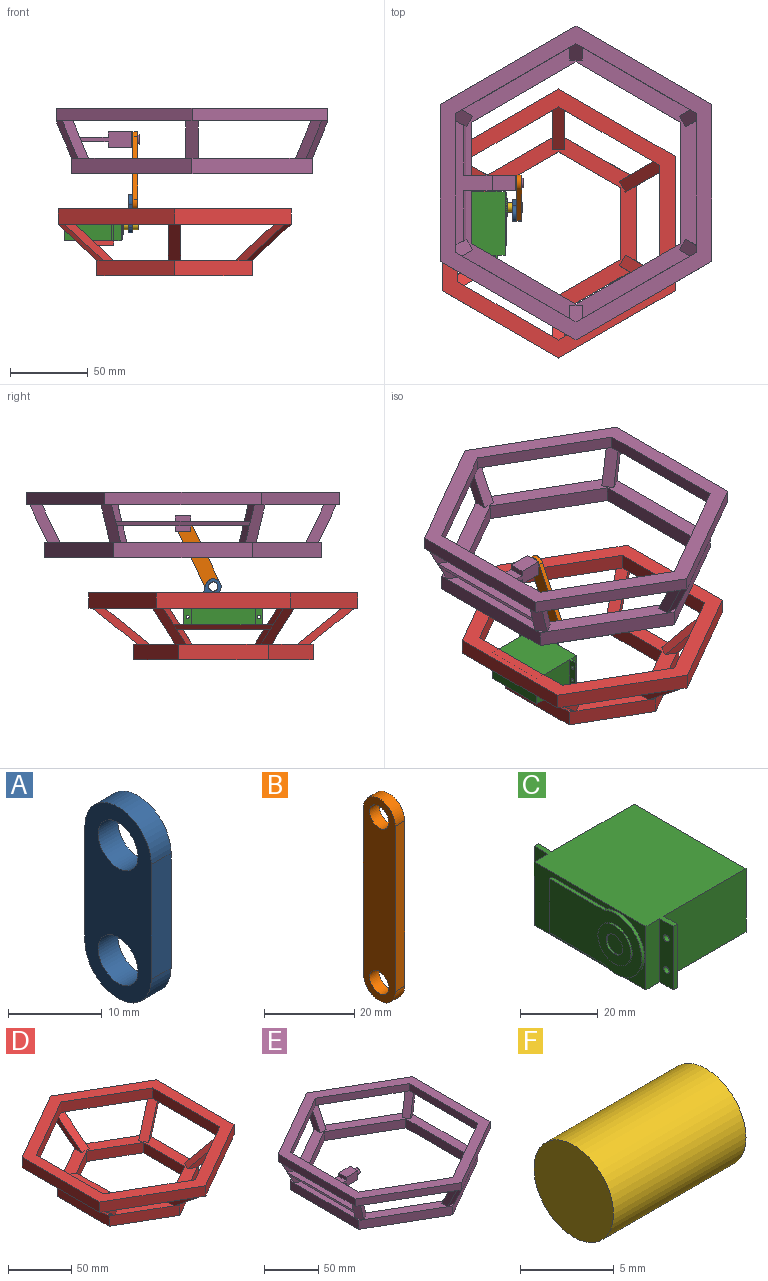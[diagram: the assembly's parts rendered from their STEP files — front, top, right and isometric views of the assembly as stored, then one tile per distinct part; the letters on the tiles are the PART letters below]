
ASSEMBLY  parts=6 mates=6
PART A: 8 faces, bbox 3x10x25 mm
  f0: plane 15x3mm, normal (0,1,0), area 45mm2, adj f1,f5,f6,f7
  f1: cylinder r=5mm len=10mm, axis (-1,0,0), area 47.1mm2, adj f0,f2,f6,f7
  f2: plane 15x3mm, normal (0,-1,0), area 45mm2, adj f1,f5,f6,f7
  f3: cylinder r=3mm len=6mm, axis (-1,0,0), area 56.5mm2, adj f6,f7
  f4: cylinder r=3mm len=6mm, axis (-1,0,0), area 56.5mm2, adj f6,f7
  f5: cylinder r=5mm len=10mm, axis (-1,0,0), area 47.1mm2, adj f0,f2,f6,f7
  f6: plane 25x10mm, normal (1,0,0), area 172mm2, adj f0,f1,f2,f3,f4,f5
  f7: plane 25x10mm, normal (-1,0,0), area 172mm2, adj f0,f1,f2,f3,f4,f5
PART B: 8 faces, bbox 3x10x55 mm
  f0: plane 45x3mm, normal (0,1,0), area 135mm2, adj f1,f5,f6,f7
  f1: cylinder r=5mm len=10mm, axis (-1,0,0), area 47.1mm2, adj f0,f2,f6,f7
  f2: plane 45x3mm, normal (0,-1,0), area 135mm2, adj f1,f5,f6,f7
  f3: cylinder r=3mm len=6mm, axis (-1,0,0), area 56.5mm2, adj f6,f7
  f4: cylinder r=3mm len=6mm, axis (-1,0,0), area 56.5mm2, adj f6,f7
  f5: cylinder r=5mm len=10mm, axis (-1,0,0), area 47.1mm2, adj f0,f2,f6,f7
  f6: plane 55x10mm, normal (1,0,0), area 472mm2, adj f0,f1,f2,f3,f4,f5
  f7: plane 55x10mm, normal (-1,0,0), area 472mm2, adj f0,f1,f2,f3,f4,f5
PART C: 27 faces, bbox 38x50.8x20 mm
  f0: plane 20x5mm, normal (0,1,0), area 100mm2, adj f2,f3,f4,f22
  f1: plane 20x5mm, normal (0,-1,0), area 100mm2, adj f2,f3,f4,f19
  f2: plane 40.8x20mm, normal (-1,0,0), area 256.4mm2, adj f0,f1,f3,f4,f8,f9,f10,f11
  f3: plane 50.8x36.5mm, normal (0,0,1), area 1504.2mm2, adj f0,f1,f2,f5,f6,f7,f17,f18
  f4: plane 50.8x36.5mm, normal (0,0,-1), area 1504.2mm2, adj f0,f1,f2,f5,f6,f7,f17,f18
  f5: plane 40.8x20mm, normal (1,0,0), area 816mm2, adj f3,f4,f6,f7
  f6: plane 30x20mm, normal (0,-1,0), area 600mm2, adj f3,f4,f5,f18
  f7: plane 30x20mm, normal (0,1,0), area 600mm2, adj f3,f4,f5,f21
  f8: plane 20x1mm, normal (0,0,1), area 20mm2, adj f2,f9,f11,f12
  f9: plane 17x1mm, normal (0,1,0), area 17mm2, adj f2,f8,f10,f12
  f10: plane 20x1mm, normal (0,0,-1), area 20mm2, adj f2,f9,f11,f12
  f11: cylinder r=9.5mm len=19mm, axis (1,0,0), area 38.6mm2, adj f2,f8,f10,f12
  f12: plane 33.74x19mm, normal (-1,0,0), area 446.5mm2, adj f8,f9,f10,f11,f13
  f13: cylinder r=6mm len=12mm, axis (1,0,0), area 18.8mm2, adj f12,f14
  f14: plane 12x12mm, normal (-1,0,0), area 84.8mm2, adj f13,f15
  f15: cylinder r=3mm len=6mm, axis (-1,0,0), area 9.4mm2, adj f14,f16
  f16: plane 6x6mm, normal (-1,0,0), area 28.3mm2, adj f15
  f17: plane 20x1.5mm, normal (0,-1,0), area 30mm2, adj f3,f4,f18,f19
  f18: plane 20x5mm, normal (1,0,0), area 93.7mm2, adj f3,f4,f6,f17,f25,f26
  f19: plane 20x5mm, normal (-1,0,0), area 93.7mm2, adj f1,f3,f4,f17,f25,f26
  f20: plane 20x1.5mm, normal (0,1,0), area 30mm2, adj f3,f4,f21,f22
  f21: plane 20x5mm, normal (1,0,0), area 93.7mm2, adj f3,f4,f7,f20,f23,f24
  f22: plane 20x5mm, normal (-1,0,0), area 93.7mm2, adj f0,f3,f4,f20,f23,f24
  f23: cylinder r=1mm len=2mm, axis (-1,0,0), area 9.4mm2, adj f21,f22
  f24: cylinder r=1mm len=2mm, axis (-1,0,0), area 9.4mm2, adj f21,f22
  f25: cylinder r=1mm len=2mm, axis (-1,0,0), area 9.4mm2, adj f18,f19
  f26: cylinder r=1mm len=2mm, axis (-1,0,0), area 9.4mm2, adj f18,f19
PART D: 136 faces, bbox 150x173.2x43 mm
  f0: plane 17.25x9.96mm, normal (-0.5,-0.87,0), area 76mm2, adj f4,f34,f36,f69
  f1: plane 18.34x10.59mm, normal (-0.5,0.87,0), area 84mm2, adj f3,f25,f27,f67
  f2: plane 17.25x9.96mm, normal (-0.5,0.87,0), area 76mm2, adj f4,f25,f27,f69
  f3: plane 168.59x150mm, normal (0,0,-1), area 4410.3mm2, adj f1,f13,f14,f15,f16,f17,f18,f19
  f4: plane 110.85x100mm, normal (0,0,1), area 2678.3mm2, adj f0,f2,f25,f26,f28,f29,f30,f34
  f5: plane 8x2.31mm, normal (0,0,1), area 9.2mm2, adj f52,f56,f65
  f6: plane 8x2.31mm, normal (0,0,-1), area 9.2mm2, adj f16,f20,f65
  f7: plane 6.93x4mm, normal (0,0,-1), area 9.2mm2, adj f22,f24,f27
  f8: plane 6.93x4mm, normal (0,0,-1), area 9.2mm2, adj f14,f18,f31
  f9: plane 6.93x4mm, normal (0,0,-1), area 9.2mm2, adj f20,f24,f36
  f10: plane 8x2.31mm, normal (0,0,-1), area 9.2mm2, adj f18,f22,f39
  f11: plane 6.93x4mm, normal (0,0,-1), area 9.2mm2, adj f14,f16,f43
  f12: plane 173.21x150mm, normal (0,0,1), area 4849.7mm2, adj f13,f14,f15,f16,f17,f18,f19,f20
  f13: plane 75.06x10mm, normal (-1,0,0), area 750.6mm2, adj f3,f12,f15,f17
  f14: plane 86.6x10mm, normal (1,0,0), area 866mm2, adj f3,f8,f11,f12,f16,f18
  f15: plane 65x37.53mm, normal (-0.5,-0.87,0), area 750.6mm2, adj f3,f12,f13,f19
  f16: plane 75x43.3mm, normal (0.5,0.87,0), area 866mm2, adj f3,f6,f11,f12,f14,f20
  f17: plane 65x37.53mm, normal (-0.5,0.87,0), area 750.6mm2, adj f3,f12,f13,f21
  f18: plane 75x43.3mm, normal (0.5,-0.87,0), area 866mm2, adj f3,f8,f10,f12,f14,f22
  f19: plane 65x37.53mm, normal (0.5,-0.87,0), area 750.6mm2, adj f3,f12,f15,f23
  f20: plane 75x43.3mm, normal (-0.5,0.87,0), area 866mm2, adj f3,f6,f9,f12,f16,f24
  f21: plane 65x37.53mm, normal (0.5,0.87,0), area 750.6mm2, adj f3,f12,f17,f23
  f22: plane 75x43.3mm, normal (-0.5,-0.87,0), area 866mm2, adj f3,f7,f10,f12,f18,f24
  f23: plane 75.06x10mm, normal (1,0,0), area 750.6mm2, adj f3,f12,f19,f21
  f24: plane 86.6x10mm, normal (-1,0,0), area 866mm2, adj f3,f7,f9,f12,f20,f22
  f25: plane 29x23mm, normal (0.54,0.31,0.78), area 295.3mm2, adj f1,f2,f3,f4,f26,f66
  f26: plane 31.93x23mm, normal (0.5,-0.87,0), area 184mm2, adj f3,f4,f25,f27
  f27: plane 29x23mm, normal (-0.54,-0.31,-0.78), area 295.3mm2, adj f1,f2,f7,f26,f32,f68
  f28: plane 31.93x23mm, normal (-0.5,-0.87,0), area 184mm2, adj f3,f4,f29,f31
  f29: plane 29x23mm, normal (-0.54,0.31,0.78), area 295.3mm2, adj f3,f4,f28,f30
  f30: plane 31.93x23mm, normal (0.5,0.87,0), area 184mm2, adj f3,f4,f29,f31
  f31: plane 29x23mm, normal (0.54,-0.31,-0.78), area 295.3mm2, adj f8,f28,f30,f37
  f32: plane 6.93x4mm, normal (0,0,1), area 9.2mm2, adj f27,f58,f60
  f33: plane 18.34x10.59mm, normal (-0.5,-0.87,0), area 84mm2, adj f3,f34,f36,f67
  f34: plane 29x23mm, normal (0.54,-0.31,0.78), area 295.3mm2, adj f0,f3,f4,f33,f35,f71
  f35: plane 31.93x23mm, normal (0.5,0.87,0), area 184mm2, adj f3,f4,f34,f36
  f36: plane 29x23mm, normal (-0.54,0.31,-0.78), area 295.3mm2, adj f0,f9,f33,f35,f38,f68
  f37: plane 6.93x4mm, normal (0,0,1), area 9.2mm2, adj f31,f49,f54
  f38: plane 6.93x4mm, normal (0,0,1), area 9.2mm2, adj f36,f56,f60
  f39: plane 28.87x23mm, normal (0,-0.62,-0.78), area 295.3mm2, adj f10,f40,f42,f47
  f40: plane 36.87x23mm, normal (-1,0,0), area 184mm2, adj f3,f4,f39,f41
  f41: plane 28.87x23mm, normal (0,0.62,0.78), area 295.3mm2, adj f3,f4,f40,f42
  f42: plane 36.87x23mm, normal (1,0,0), area 184mm2, adj f3,f4,f39,f41
  f43: plane 29x23mm, normal (0.54,0.31,-0.78), area 295.3mm2, adj f11,f44,f46,f50
  f44: plane 31.93x23mm, normal (0.5,-0.87,0), area 184mm2, adj f3,f4,f43,f45
  f45: plane 29x23mm, normal (-0.54,-0.31,0.78), area 295.3mm2, adj f3,f4,f44,f46
  f46: plane 31.93x23mm, normal (-0.5,0.87,0), area 184mm2, adj f3,f4,f43,f45
  f47: plane 8x2.31mm, normal (0,0,1), area 9.2mm2, adj f39,f54,f58
  f48: plane 115.47x100mm, normal (0,0,-1), area 3117.7mm2, adj f49,f51,f52,f53,f54,f55,f56,f57
  f49: plane 57.74x10mm, normal (1,0,0), area 577.4mm2, adj f4,f37,f48,f50,f52,f54
  f50: plane 6.93x4mm, normal (0,0,1), area 9.2mm2, adj f43,f49,f52
  f51: plane 46.19x10mm, normal (-1,0,0), area 461.9mm2, adj f4,f48,f53,f55
  f52: plane 50x28.87mm, normal (0.5,0.87,0), area 577.4mm2, adj f4,f5,f48,f49,f50,f56
  f53: plane 40x23.09mm, normal (-0.5,-0.87,0), area 461.9mm2, adj f4,f48,f51,f57
  f54: plane 50x28.87mm, normal (0.5,-0.87,0), area 577.4mm2, adj f4,f37,f47,f48,f49,f58
  f55: plane 40x23.09mm, normal (-0.5,0.87,0), area 461.9mm2, adj f4,f48,f51,f59
  f56: plane 50x28.87mm, normal (-0.5,0.87,0), area 577.4mm2, adj f4,f5,f38,f48,f52,f60
  f57: plane 40x23.09mm, normal (0.5,-0.87,0), area 461.9mm2, adj f4,f48,f53,f61
  f58: plane 50x28.87mm, normal (-0.5,-0.87,0), area 577.4mm2, adj f4,f32,f47,f48,f54,f60
  f59: plane 40x23.09mm, normal (0.5,0.87,0), area 461.9mm2, adj f4,f48,f55,f61
  f60: plane 57.74x10mm, normal (-1,0,0), area 577.4mm2, adj f4,f32,f38,f48,f56,f58
  f61: plane 46.19x10mm, normal (1,0,0), area 461.9mm2, adj f4,f48,f57,f59
  f62: plane 36.87x23mm, normal (-1,0,0), area 184mm2, adj f3,f4,f63,f65
  f63: plane 28.87x23mm, normal (0,-0.62,0.78), area 295.3mm2, adj f3,f4,f62,f64
  f64: plane 36.87x23mm, normal (1,0,0), area 184mm2, adj f3,f4,f63,f65
  f65: plane 28.87x23mm, normal (0,0.62,-0.78), area 295.3mm2, adj f5,f6,f62,f64
  f66: plane 17.59x10.15mm, normal (0.5,-0.87,0), area 55.3mm2, adj f25,f67,f69,f70
  f67: plane 64.19x24.52mm, normal (0,0,1), area 1226.6mm2, adj f1,f33,f66,f68,f70,f71
  f68: plane 64.19x3.26mm, normal (-0.68,0,-0.74), area 276.1mm2, adj f27,f36,f67,f69
  f69: plane 60.42x21.25mm, normal (0,0,-1), area 1023.4mm2, adj f0,f2,f66,f68,f70,f71
  f70: plane 35.88x3mm, normal (1,0,0), area 107.6mm2, adj f66,f67,f69,f71
  f71: plane 17.59x10.15mm, normal (0.5,0.87,0), area 55.3mm2, adj f34,f67,f69,f70
  f72: plane 4x1.58mm, normal (0,0,1), area 6.3mm2, adj f74,f75,f76,f77
  f73: plane 4x1.58mm, normal (0,0,-1), area 6.3mm2, adj f74,f75,f76,f77
  f74: plane 25.43x19mm, normal (1,0,0), area 30mm2, adj f72,f73,f75,f77
  f75: plane 23.85x19mm, normal (0,0.62,-0.78), area 122mm2, adj f72,f73,f74,f76
  f76: plane 25.43x19mm, normal (-1,0,0), area 30mm2, adj f72,f73,f75,f77
  f77: plane 23.85x19mm, normal (0,-0.62,0.78), area 122mm2, adj f72,f73,f74,f76
  f78: plane 84.29x6mm, normal (-1,0,0), area 505.8mm2, adj f80,f82,f89,f91
  f79: plane 77.37x6mm, normal (1,0,0), area 464.2mm2, adj f81,f83,f89,f91
  f80: plane 73x42.15mm, normal (-0.5,-0.87,0), area 505.8mm2, adj f78,f84,f89,f91
  f81: plane 67x38.68mm, normal (0.5,0.87,0), area 464.2mm2, adj f79,f85,f89,f91
  f82: plane 73x42.15mm, normal (-0.5,0.87,0), area 505.8mm2, adj f78,f86,f89,f91
  f83: plane 67x38.68mm, normal (0.5,-0.87,0), area 464.2mm2, adj f79,f87,f89,f91
  f84: plane 73x42.15mm, normal (0.5,-0.87,0), area 505.8mm2, adj f80,f88,f89,f91
  f85: plane 67x38.68mm, normal (-0.5,0.87,0), area 464.2mm2, adj f81,f89,f90,f91
  f86: plane 73x42.15mm, normal (0.5,0.87,0), area 505.8mm2, adj f82,f88,f89,f91
  f87: plane 67x38.68mm, normal (-0.5,-0.87,0), area 464.2mm2, adj f83,f89,f90,f91
  f88: plane 84.29x6mm, normal (1,0,0), area 505.8mm2, adj f84,f86,f89,f91
  f89: plane 168.59x146mm, normal (0,0,1), area 2909.8mm2, adj f78,f79,f80,f81,f82,f83,f84,f85
  f90: plane 77.37x6mm, normal (-1,0,0), area 464.2mm2, adj f85,f87,f89,f91
  f91: plane 168.59x146mm, normal (0,0,-1), area 2909.8mm2, adj f78,f79,f80,f81,f82,f83,f84,f85
  f92: plane 4.25x3.37mm, normal (0,0,-1), area 6.3mm2, adj f94,f95,f96,f97
  f93: plane 4.25x3.37mm, normal (0,0,1), area 6.3mm2, adj f94,f95,f96,f97
  f94: plane 22.02x19mm, normal (0.5,-0.87,0), area 30mm2, adj f92,f93,f95,f97
  f95: plane 22.65x19mm, normal (-0.54,-0.31,-0.78), area 122mm2, adj f92,f93,f94,f96
  f96: plane 22.02x19mm, normal (-0.5,0.87,0), area 30mm2, adj f92,f93,f95,f97
  f97: plane 22.65x19mm, normal (0.54,0.31,0.78), area 122mm2, adj f92,f93,f94,f96
  f98: plane 4.25x3.37mm, normal (0,0,-1), area 6.3mm2, adj f100,f101,f102,f103
  f99: plane 4.25x3.37mm, normal (0,0,1), area 6.3mm2, adj f100,f101,f102,f103
  f100: plane 22.02x19mm, normal (0.5,0.87,0), area 30mm2, adj f98,f99,f101,f103
  f101: plane 22.65x19mm, normal (0.54,-0.31,-0.78), area 122mm2, adj f98,f99,f100,f102
  f102: plane 22.02x19mm, normal (-0.5,-0.87,0), area 30mm2, adj f98,f99,f101,f103
  f103: plane 22.65x19mm, normal (-0.54,0.31,0.78), area 122mm2, adj f98,f99,f100,f102
  f104: plane 4.25x3.37mm, normal (0,0,1), area 6.3mm2, adj f106,f107,f108,f109
  f105: plane 4.25x3.37mm, normal (0,0,-1), area 6.3mm2, adj f106,f107,f108,f109
  f106: plane 22.02x19mm, normal (0.5,0.87,0), area 30mm2, adj f104,f105,f107,f109
  f107: plane 22.65x19mm, normal (-0.54,0.31,-0.78), area 122mm2, adj f104,f105,f106,f108
  f108: plane 22.02x19mm, normal (-0.5,-0.87,0), area 30mm2, adj f104,f105,f107,f109
  f109: plane 22.65x19mm, normal (0.54,-0.31,0.78), area 122mm2, adj f104,f105,f106,f108
  f110: plane 4x1.58mm, normal (0,0,-1), area 6.3mm2, adj f112,f113,f114,f115
  f111: plane 4x1.58mm, normal (0,0,1), area 6.3mm2, adj f112,f113,f114,f115
  f112: plane 23.85x19mm, normal (0,0.62,0.78), area 122mm2, adj f110,f111,f113,f115
  f113: plane 25.43x19mm, normal (1,0,0), area 30mm2, adj f110,f111,f112,f114
  f114: plane 23.85x19mm, normal (0,-0.62,-0.78), area 122mm2, adj f110,f111,f113,f115
  f115: plane 25.43x19mm, normal (-1,0,0), area 30mm2, adj f110,f111,f112,f114
  f116: plane 4.25x3.37mm, normal (0,0,-1), area 6.3mm2, adj f118,f119,f120,f121
  f117: plane 4.25x3.37mm, normal (0,0,1), area 6.3mm2, adj f118,f119,f120,f121
  f118: plane 22.65x19mm, normal (-0.54,-0.31,0.78), area 122mm2, adj f116,f117,f119,f121
  f119: plane 22.02x19mm, normal (-0.5,0.87,0), area 30mm2, adj f116,f117,f118,f120
  f120: plane 22.65x19mm, normal (0.54,0.31,-0.78), area 122mm2, adj f116,f117,f119,f121
  f121: plane 22.02x19mm, normal (0.5,-0.87,0), area 30mm2, adj f116,f117,f118,f120
  f122: plane 48.5x6mm, normal (1,0,0), area 291mm2, adj f124,f126,f133,f135
  f123: plane 55.43x6mm, normal (-1,0,0), area 332.6mm2, adj f125,f127,f133,f135
  f124: plane 42x24.25mm, normal (0.5,0.87,0), area 291mm2, adj f122,f128,f133,f135
  f125: plane 48x27.71mm, normal (-0.5,-0.87,0), area 332.6mm2, adj f123,f129,f133,f135
  f126: plane 42x24.25mm, normal (0.5,-0.87,0), area 291mm2, adj f122,f130,f133,f135
  f127: plane 48x27.71mm, normal (-0.5,0.87,0), area 332.6mm2, adj f123,f131,f133,f135
  f128: plane 42x24.25mm, normal (-0.5,0.87,0), area 291mm2, adj f124,f132,f133,f135
  f129: plane 48x27.71mm, normal (0.5,-0.87,0), area 332.6mm2, adj f125,f133,f134,f135
  f130: plane 42x24.25mm, normal (-0.5,-0.87,0), area 291mm2, adj f126,f132,f133,f135
  f131: plane 48x27.71mm, normal (0.5,0.87,0), area 332.6mm2, adj f127,f133,f134,f135
  f132: plane 48.5x6mm, normal (-1,0,0), area 291mm2, adj f128,f130,f133,f135
  f133: plane 110.85x96mm, normal (0,0,-1), area 1870.6mm2, adj f122,f123,f124,f125,f126,f127,f128,f129
  f134: plane 55.43x6mm, normal (1,0,0), area 332.6mm2, adj f129,f131,f133,f135
  f135: plane 110.85x96mm, normal (0,0,1), area 1870.6mm2, adj f122,f123,f124,f125,f126,f127,f128,f129
PART E: 146 faces, bbox 175x202.1x42.1 mm
  f0: plane 85.29x27.79mm, normal (0,0,-1), area 1031.7mm2, adj f2,f3,f5,f6,f7,f8,f9,f11
  f1: plane 86.74x29.04mm, normal (0,0,1), area 1060.1mm2, adj f2,f3,f5,f6,f7,f8,f9,f10
  f2: plane 5.25x3.03mm, normal (0.5,-0.87,0), area 13.9mm2, adj f0,f1,f9,f22
  f3: plane 33.12x10mm, normal (0,-1,0), area 202.5mm2, adj f0,f1,f4,f9,f76,f77,f78,f79
  f4: plane 10x10mm, normal (1,0,0), area 71.7mm2, adj f3,f6,f76,f79,f80
  f5: plane 86.74x3mm, normal (-0.92,0,-0.39), area 279.6mm2, adj f0,f1,f20,f26
  f6: plane 33.12x10mm, normal (0,1,0), area 202.5mm2, adj f0,f1,f4,f8,f76,f77,f78,f79
  f7: plane 5.25x3.03mm, normal (0.5,0.87,0), area 13.9mm2, adj f0,f1,f8,f27
  f8: plane 32.06x3mm, normal (0.92,0,0.39), area 103mm2, adj f0,f1,f6,f7
  f9: plane 32.06x3mm, normal (0.92,0,0.39), area 103mm2, adj f0,f1,f2,f3
  f10: plane 11.31x10.5mm, normal (-0.5,0.87,0), area 84mm2, adj f1,f19,f20,f22
  f11: plane 11.29x10.45mm, normal (-0.5,-0.87,0), area 83.6mm2, adj f0,f17,f26,f27
  f12: plane 11.31x10.5mm, normal (-0.5,-0.87,0), area 84mm2, adj f1,f19,f26,f27
  f13: plane 23.95x14mm, normal (0.78,0.45,-0.43), area 212.7mm2, adj f14,f16,f18,f25
  f14: plane 23.95x16.93mm, normal (-0.5,0.87,0), area 191.6mm2, adj f13,f15,f17,f19
  f15: plane 23.95x14mm, normal (-0.78,-0.45,0.43), area 212.7mm2, adj f14,f16,f17,f19
  f16: plane 23.95x16.93mm, normal (0.5,-0.87,0), area 191.6mm2, adj f13,f15,f17,f19
  f17: plane 174.36x155mm, normal (0,0,1), area 4583.5mm2, adj f11,f14,f15,f16,f21,f22,f23,f27
  f18: plane 6.93x4mm, normal (0,0,1), area 9.2mm2, adj f13,f49,f51
  f19: plane 197.45x175mm, normal (0,0,-1), area 5276.3mm2, adj f10,f12,f14,f15,f16,f21,f22,f27
  f20: plane 23.95x14mm, normal (-0.78,-0.45,-0.43), area 212.7mm2, adj f5,f10,f21,f23,f24,f30
  f21: plane 23.95x16.93mm, normal (0.5,-0.87,0), area 191.6mm2, adj f17,f19,f20,f22
  f22: plane 23.95x14mm, normal (0.78,0.45,0.43), area 212.7mm2, adj f2,f10,f17,f19,f21,f23
  f23: plane 11.29x10.45mm, normal (-0.5,0.87,0), area 83.6mm2, adj f0,f17,f20,f22
  f24: plane 6.93x4mm, normal (0,0,1), area 9.2mm2, adj f20,f57,f59
  f25: plane 6.93x4mm, normal (0,0,-1), area 9.2mm2, adj f13,f63,f66
  f26: plane 23.95x14mm, normal (-0.78,0.45,-0.43), area 212.7mm2, adj f5,f11,f12,f28,f29,f36
  f27: plane 23.95x14mm, normal (0.78,-0.45,0.43), area 212.7mm2, adj f7,f11,f12,f17,f19,f28
  f28: plane 23.95x16.93mm, normal (0.5,0.87,0), area 191.6mm2, adj f17,f19,f26,f27
  f29: plane 6.93x4mm, normal (0,0,1), area 9.2mm2, adj f26,f55,f59
  f30: plane 6.93x4mm, normal (0,0,-1), area 9.2mm2, adj f20,f72,f74
  f31: plane 23.95x11.55mm, normal (0,0.9,-0.43), area 212.7mm2, adj f32,f34,f35,f42
  f32: plane 23.95x19.55mm, normal (-1,0,0), area 191.6mm2, adj f17,f19,f31,f33
  f33: plane 23.95x11.55mm, normal (0,-0.9,0.43), area 212.7mm2, adj f17,f19,f32,f34
  f34: plane 23.95x19.55mm, normal (1,0,0), area 191.6mm2, adj f17,f19,f31,f33
  f35: plane 8x2.31mm, normal (0,0,1), area 9.2mm2, adj f31,f51,f55
  f36: plane 6.93x4mm, normal (0,0,-1), area 9.2mm2, adj f26,f70,f74
  f37: plane 23.95x11.55mm, normal (0,-0.9,-0.43), area 212.7mm2, adj f38,f40,f41,f61
  f38: plane 23.95x19.55mm, normal (1,0,0), area 191.6mm2, adj f17,f19,f37,f39
  f39: plane 23.95x11.55mm, normal (0,0.9,0.43), area 212.7mm2, adj f17,f19,f38,f40
  f40: plane 23.95x19.55mm, normal (-1,0,0), area 191.6mm2, adj f17,f19,f37,f39
  f41: plane 8x2.31mm, normal (0,0,1), area 9.2mm2, adj f37,f53,f57
  f42: plane 8x2.31mm, normal (0,0,-1), area 9.2mm2, adj f31,f66,f70
  f43: plane 23.95x14mm, normal (0.78,-0.45,-0.43), area 212.7mm2, adj f44,f46,f47,f62
  f44: plane 23.95x16.93mm, normal (0.5,0.87,0), area 191.6mm2, adj f17,f19,f43,f45
  f45: plane 23.95x14mm, normal (-0.78,0.45,0.43), area 212.7mm2, adj f17,f19,f44,f46
  f46: plane 23.95x16.93mm, normal (-0.5,-0.87,0), area 191.6mm2, adj f17,f19,f43,f45
  f47: plane 6.93x4mm, normal (0,0,1), area 9.2mm2, adj f43,f49,f53
  f48: plane 178.98x155mm, normal (0,0,-1), area 5022.9mm2, adj f49,f50,f51,f52,f53,f54,f55,f56
  f49: plane 89.49x10mm, normal (1,0,0), area 894.9mm2, adj f17,f18,f47,f48,f51,f53
  f50: plane 77.94x10mm, normal (-1,0,0), area 779.4mm2, adj f17,f48,f52,f54
  f51: plane 77.5x44.74mm, normal (0.5,0.87,0), area 894.9mm2, adj f17,f18,f35,f48,f49,f55
  f52: plane 67.5x38.97mm, normal (-0.5,-0.87,0), area 779.4mm2, adj f17,f48,f50,f56
  f53: plane 77.5x44.74mm, normal (0.5,-0.87,0), area 894.9mm2, adj f17,f41,f47,f48,f49,f57
  f54: plane 67.5x38.97mm, normal (-0.5,0.87,0), area 779.4mm2, adj f17,f48,f50,f58
  f55: plane 77.5x44.74mm, normal (-0.5,0.87,0), area 894.9mm2, adj f17,f29,f35,f48,f51,f59
  f56: plane 67.5x38.97mm, normal (0.5,-0.87,0), area 779.4mm2, adj f17,f48,f52,f60
  f57: plane 77.5x44.74mm, normal (-0.5,-0.87,0), area 894.9mm2, adj f17,f24,f41,f48,f53,f59
  f58: plane 67.5x38.97mm, normal (0.5,0.87,0), area 779.4mm2, adj f17,f48,f54,f60
  f59: plane 89.49x10mm, normal (-1,0,0), area 894.9mm2, adj f17,f24,f29,f48,f55,f57
  f60: plane 77.94x10mm, normal (1,0,0), area 779.4mm2, adj f17,f48,f56,f58
  f61: plane 8x2.31mm, normal (0,0,-1), area 9.2mm2, adj f37,f68,f72
  f62: plane 6.93x4mm, normal (0,0,-1), area 9.2mm2, adj f43,f63,f68
  f63: plane 101.04x8.1mm, normal (1,0,0), area 818.7mm2, adj f19,f25,f62,f64,f66,f68
  f64: plane 202.07x175mm, normal (0,0,1), area 5715.8mm2, adj f63,f65,f66,f67,f68,f69,f70,f71
  f65: plane 89.49x8.1mm, normal (-1,0,0), area 725.2mm2, adj f19,f64,f67,f69
  f66: plane 87.5x50.52mm, normal (0.5,0.87,0), area 818.7mm2, adj f19,f25,f42,f63,f64,f70
  f67: plane 77.5x44.74mm, normal (-0.5,-0.87,0), area 725.2mm2, adj f19,f64,f65,f71
  f68: plane 87.5x50.52mm, normal (0.5,-0.87,0), area 818.7mm2, adj f19,f61,f62,f63,f64,f72
  f69: plane 77.5x44.74mm, normal (-0.5,0.87,0), area 725.2mm2, adj f19,f64,f65,f73
  f70: plane 87.5x50.52mm, normal (-0.5,0.87,0), area 818.7mm2, adj f19,f36,f42,f64,f66,f74
  f71: plane 77.5x44.74mm, normal (0.5,-0.87,0), area 725.2mm2, adj f19,f64,f67,f75
  f72: plane 87.5x50.52mm, normal (-0.5,-0.87,0), area 818.7mm2, adj f19,f30,f61,f64,f68,f74
  f73: plane 77.5x44.74mm, normal (0.5,0.87,0), area 725.2mm2, adj f19,f64,f69,f75
  f74: plane 101.04x8.1mm, normal (-1,0,0), area 818.7mm2, adj f19,f30,f36,f64,f70,f72
  f75: plane 89.49x8.1mm, normal (1,0,0), area 725.2mm2, adj f19,f64,f71,f73
  f76: plane 15x10mm, normal (0,0,1), area 150mm2, adj f3,f4,f6,f77
  f77: plane 10x3.5mm, normal (-1,0,0), area 35mm2, adj f1,f3,f6,f76
  f78: plane 10x3.5mm, normal (-1,0,0), area 35mm2, adj f0,f3,f6,f79
  f79: plane 15x10mm, normal (0,0,-1), area 150mm2, adj f3,f4,f6,f78
  f80: cylinder r=3mm len=6mm, axis (-1,0,0), area 94.2mm2, adj f4,f81
  f81: plane 6x6mm, normal (1,0,0), area 28.3mm2, adj f80
  f82: plane 5.24x5.08mm, normal (0,0,1), area 14.2mm2, adj f84,f85,f86,f87
  f83: plane 5.24x5.08mm, normal (0,0,-1), area 14.2mm2, adj f84,f85,f86,f87
  f84: plane 19.95x10.33mm, normal (-0.78,-0.45,0.43), area 88.6mm2, adj f82,f83,f85,f87
  f85: plane 19.95x11.41mm, normal (0.5,-0.87,0), area 71mm2, adj f82,f83,f84,f86
  f86: plane 19.95x10.33mm, normal (0.78,0.45,-0.43), area 88.6mm2, adj f82,f83,f85,f87
  f87: plane 19.95x11.41mm, normal (-0.5,0.87,0), area 71mm2, adj f82,f83,f84,f86
  f88: plane 5.24x5.08mm, normal (0,0,1), area 14.2mm2, adj f90,f91,f92,f93
  f89: plane 5.24x5.08mm, normal (0,0,-1), area 14.2mm2, adj f90,f91,f92,f93
  f90: plane 19.95x10.33mm, normal (0.78,0.45,0.43), area 88.6mm2, adj f88,f89,f91,f93
  f91: plane 19.95x11.41mm, normal (-0.5,0.87,0), area 71mm2, adj f88,f89,f90,f92
  f92: plane 19.95x10.33mm, normal (-0.78,-0.45,-0.43), area 88.6mm2, adj f88,f89,f91,f93
  f93: plane 19.95x11.41mm, normal (0.5,-0.87,0), area 71mm2, adj f88,f89,f90,f92
  f94: plane 5.24x5.08mm, normal (0,0,1), area 14.2mm2, adj f96,f97,f98,f99
  f95: plane 5.24x5.08mm, normal (0,0,-1), area 14.2mm2, adj f96,f97,f98,f99
  f96: plane 19.95x10.33mm, normal (0.78,-0.45,0.43), area 88.6mm2, adj f94,f95,f97,f99
  f97: plane 19.95x11.41mm, normal (0.5,0.87,0), area 71mm2, adj f94,f95,f96,f98
  f98: plane 19.95x10.33mm, normal (-0.78,0.45,-0.43), area 88.6mm2, adj f94,f95,f97,f99
  f99: plane 19.95x11.41mm, normal (-0.5,-0.87,0), area 71mm2, adj f94,f95,f96,f98
  f100: plane 4x3.56mm, normal (0,0,1), area 14.2mm2, adj f102,f103,f104,f105
  f101: plane 4x3.56mm, normal (0,0,-1), area 14.2mm2, adj f102,f103,f104,f105
  f102: plane 19.95x9.62mm, normal (0,-0.9,0.43), area 88.6mm2, adj f100,f101,f103,f105
  f103: plane 19.95x13.18mm, normal (1,0,0), area 71mm2, adj f100,f101,f102,f104
  f104: plane 19.95x9.62mm, normal (0,0.9,-0.43), area 88.6mm2, adj f100,f101,f103,f105
  f105: plane 19.95x13.18mm, normal (-1,0,0), area 71mm2, adj f100,f101,f102,f104
  f106: plane 4x3.56mm, normal (0,0,1), area 14.2mm2, adj f108,f109,f110,f111
  f107: plane 4x3.56mm, normal (0,0,-1), area 14.2mm2, adj f108,f109,f110,f111
  f108: plane 19.95x9.62mm, normal (0,0.9,0.43), area 88.6mm2, adj f106,f107,f109,f111
  f109: plane 19.95x13.18mm, normal (-1,0,0), area 71mm2, adj f106,f107,f108,f110
  f110: plane 19.95x9.62mm, normal (0,-0.9,-0.43), area 88.6mm2, adj f106,f107,f109,f111
  f111: plane 19.95x13.18mm, normal (1,0,0), area 71mm2, adj f106,f107,f108,f110
  f112: plane 5.24x5.08mm, normal (0,0,1), area 14.2mm2, adj f114,f115,f116,f117
  f113: plane 5.24x5.08mm, normal (0,0,-1), area 14.2mm2, adj f114,f115,f116,f117
  f114: plane 19.95x10.33mm, normal (-0.78,0.45,0.43), area 88.6mm2, adj f112,f113,f115,f117
  f115: plane 19.95x11.41mm, normal (-0.5,-0.87,0), area 71mm2, adj f112,f113,f114,f116
  f116: plane 19.95x10.33mm, normal (0.78,-0.45,-0.43), area 88.6mm2, adj f112,f113,f115,f117
  f117: plane 19.95x11.41mm, normal (0.5,0.87,0), area 71mm2, adj f112,f113,f114,f116
  f118: plane 80.25x6mm, normal (1,0,0), area 481.5mm2, adj f120,f122,f129,f131
  f119: plane 87.18x6mm, normal (-1,0,0), area 523.1mm2, adj f121,f123,f129,f131
  f120: plane 69.5x40.13mm, normal (0.5,0.87,0), area 481.5mm2, adj f118,f124,f129,f131
  f121: plane 75.5x43.59mm, normal (-0.5,-0.87,0), area 523.1mm2, adj f119,f125,f129,f131
  f122: plane 69.5x40.13mm, normal (0.5,-0.87,0), area 481.5mm2, adj f118,f126,f129,f131
  f123: plane 75.5x43.59mm, normal (-0.5,0.87,0), area 523.1mm2, adj f119,f127,f129,f131
  f124: plane 69.5x40.13mm, normal (-0.5,0.87,0), area 481.5mm2, adj f120,f128,f129,f131
  f125: plane 75.5x43.59mm, normal (0.5,-0.87,0), area 523.1mm2, adj f121,f129,f130,f131
  f126: plane 69.5x40.13mm, normal (-0.5,-0.87,0), area 481.5mm2, adj f122,f128,f129,f131
  f127: plane 75.5x43.59mm, normal (0.5,0.87,0), area 523.1mm2, adj f123,f129,f130,f131
  f128: plane 80.25x6mm, normal (-1,0,0), area 481.5mm2, adj f124,f126,f129,f131
  f129: plane 174.36x151mm, normal (0,0,-1), area 3013.8mm2, adj f118,f119,f120,f121,f122,f123,f124,f125
  f130: plane 87.18x6mm, normal (1,0,0), area 523.1mm2, adj f125,f127,f129,f131
  f131: plane 174.36x151mm, normal (0,0,1), area 3013.8mm2, adj f118,f119,f120,f121,f122,f123,f124,f125
  f132: plane 91.8x4.1mm, normal (1,0,0), area 376.7mm2, adj f134,f136,f143,f145
  f133: plane 98.73x4.1mm, normal (-1,0,0), area 405.1mm2, adj f135,f137,f143,f145
  f134: plane 79.5x45.9mm, normal (0.5,0.87,0), area 376.7mm2, adj f132,f138,f143,f145
  f135: plane 85.5x49.36mm, normal (-0.5,-0.87,0), area 405.1mm2, adj f133,f139,f143,f145
  f136: plane 79.5x45.9mm, normal (0.5,-0.87,0), area 376.7mm2, adj f132,f140,f143,f145
  f137: plane 85.5x49.36mm, normal (-0.5,0.87,0), area 405.1mm2, adj f133,f141,f143,f145
  f138: plane 79.5x45.9mm, normal (-0.5,0.87,0), area 376.7mm2, adj f134,f142,f143,f145
  f139: plane 85.5x49.36mm, normal (0.5,-0.87,0), area 405.1mm2, adj f135,f143,f144,f145
  f140: plane 79.5x45.9mm, normal (-0.5,-0.87,0), area 376.7mm2, adj f136,f142,f143,f145
  f141: plane 85.5x49.36mm, normal (0.5,0.87,0), area 405.1mm2, adj f137,f143,f144,f145
  f142: plane 91.8x4.1mm, normal (-1,0,0), area 376.7mm2, adj f138,f140,f143,f145
  f143: plane 197.45x171mm, normal (0,0,-1), area 3429.5mm2, adj f132,f133,f134,f135,f136,f137,f138,f139
  f144: plane 98.73x4.1mm, normal (1,0,0), area 405.1mm2, adj f139,f141,f143,f145
  f145: plane 197.45x171mm, normal (0,0,1), area 3429.5mm2, adj f132,f133,f134,f135,f136,f137,f138,f139
PART F: 3 faces, bbox 10x6x6 mm
  f0: cylinder r=3mm len=10mm, axis (1,0,0), area 188.5mm2, adj f1,f2
  f1: plane 6x6mm, normal (-1,0,0), area 28.3mm2, adj f0
  f2: plane 6x6mm, normal (1,0,0), area 28.3mm2, adj f0
PLACE A rot(axis=(1,0,0),15.1deg) t=(-40.47,-5.1,17.32)mm
PLACE B rot(axis=(0,-0.97,0.22),180deg) t=(-34.47,-5.1,17.32)mm
PLACE C rot(axis=(0,0,1),180deg) t=(-44.97,-11.6,-7.21)mm
PLACE D t=(-10.61,-11.6,8.29)mm fixed
PLACE E rot(axis=(-1,0,0),0deg) t=(0.6,14.41,30.92)mm
PLACE F rot(axis=(0,-1,0),180deg) t=(-45.47,9.2,12.89)mm
MATE fastened F.f0 <-> C.f13  axis (-1,0,0) through (-43.97,-1.2,2.84)mm
MATE fastened C.f4 <-> D.f67  axis (0,0,-1) through (-63.09,-11.6,-7.21)mm
MATE parallel D.f12 <-> E.f48  axis (0,0,1) through (-10.61,-11.6,13.29)mm
MATE revolute F.f0 <-> A.f4  axis (-1,0,0) through (-38.97,-1.2,2.84)mm
MATE revolute E.f80 <-> B.f4  axis (-1,0,0) through (-35.97,14.41,57.87)mm
MATE revolute B.f1 <-> A.f1  axis (-1,0,0) through (-37.47,-5.1,17.32)mm
